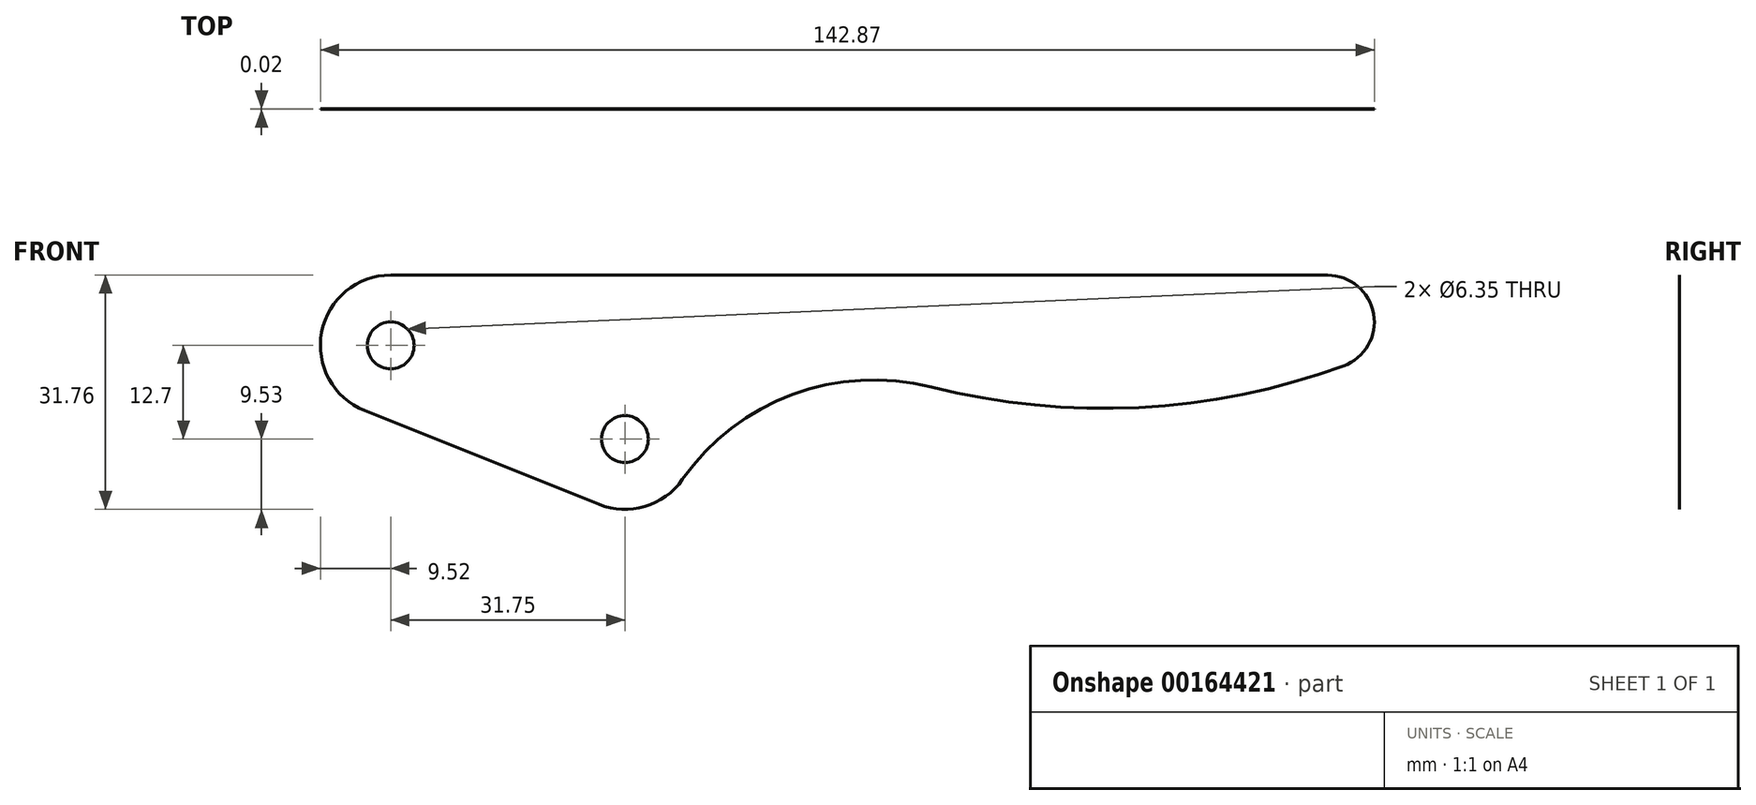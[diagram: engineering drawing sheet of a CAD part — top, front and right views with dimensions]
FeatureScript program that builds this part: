
annotation { "Feature Type Name" : "Feature", "Feature Type Description" : "" }
export const myFeature = defineFeature(function(context is Context, id is Id, definition is map)
    precondition{}
    {
        {
            var Q0;
            Q0=qCreatedBy(makeId("Front.planeOp"),FACE);
            var sketch = newSketch(context, id + "F0", { "sketchPlane" : qUnion([Q0])});
            skCircle(sketch, "E0", {"center": v(0, 0) * mm, "radius": 3.18 * mm});
            skArc(sketch, "E1", {"start": v(0, 9.53) * mm, "mid": v(-9.35, 1.8) * mm, "end": v(-3.54, -8.84) * mm});
            skArc(sketch, "E2", {"start": v(129.17, -2.8) * mm, "mid": v(133.25, 4.28) * mm, "end": v(127, 9.53) * mm});
            skLineSegment(sketch, "E3", {"start": v(127, 9.53) * mm, "end": v(0, 9.53) * mm});
            skArc(sketch, "E4", {"start": v(73.3, -5.64) * mm, "mid": v(101.45, -8.41) * mm, "end": v(129.17, -2.8) * mm});
            skLineSegment(sketch, "E5", {"start": v(127, 3.18) * mm, "end": v(129.17, -2.8) * mm, "construction": true});
            skLineSegment(sketch, "E6", {"start": v(127, 3.18) * mm, "end": v(127, 9.53) * mm, "construction": true});
            skArc(sketch, "E7", {"start": v(73.3, -5.64) * mm, "mid": v(54.47, -6.66) * mm, "end": v(39.54, -18.18) * mm});
            skLineSegment(sketch, "E8", {"start": v(-3.54, -8.84) * mm, "end": v(28.21, -21.54) * mm});
            skArc(sketch, "E9", {"start": v(28.21, -21.54) * mm, "mid": v(34.46, -21.83) * mm, "end": v(39.54, -18.18) * mm});
            skCircle(sketch, "E10", {"center": v(31.75, -12.7) * mm, "radius": 3.18 * mm});
            skLineSegment(sketch, "E11", {"start": v(0, 0) * mm, "end": v(31.75, -12.7) * mm, "construction": true});
            skSolve(sketch);
        }
        {
            var Q0;
            Q0 = qSketchRegion(id + "F0", true);
            extrude(context, id + "F1", {"entities" : qUnion([Q0]), "depth" : 5 / 203.2 * mm});
        }
        {
            var Q0;
            Q0=makeQuery(id+"F1.opExtrude","SWEPT_FACE",FACE,{"disambiguationData":[OSD([sQuery(id+"F0.wireOp",EDGE,"E8")])]});
            var sketch = newSketch(context, id + "F2", { "sketchPlane" : qUnion([Q0])});
            skLineSegment(sketch, "E12.bottom", {"start": v(-21, 4.64) * mm, "end": v(55.2, 4.64) * mm});
            skLineSegment(sketch, "E12.top", {"start": v(-21, 11.24) * mm, "end": v(55.2, 11.24) * mm});
            skLineSegment(sketch, "E12.left", {"start": v(-21, 4.64) * mm, "end": v(-21, 11.24) * mm});
            skLineSegment(sketch, "E12.right", {"start": v(55.2, 4.64) * mm, "end": v(55.2, 11.24) * mm});
            skPoint(sketch, "E12.middle", {"position": v(17.1, 7.94) * mm});
            skLineSegment(sketch, "E13", {"start": v(17.1, 7.94) * mm, "end": v(17.1, 15.88) * mm, "construction": true});
            skSolve(sketch);
        }
        {
            var Q0;
            Q0 = qSketchRegion(id + "F2", true);
            extrude(context, id + "F3", {"entities" : qUnion([Q0]), "operationType" : NewBodyOperationType.REMOVE, "oppositeDirection" : true, "depth" : 25.4 * mm});
        }
        {
            var Q0;
            Q0=qCreatedBy(makeId("Top.planeOp"),FACE);
            cPlane(context, id + "F5", {"entities" : qUnion([Q0]), "cplaneType" : CPlaneType.OFFSET, "offset" : 25.4 * mm, "oppositeDirection" : true, "width" : 152.4 * mm, "height" : 152.4 * mm});
        }
    });
